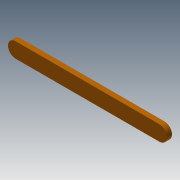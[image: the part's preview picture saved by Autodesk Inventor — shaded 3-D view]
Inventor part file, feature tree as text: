
AUTODESK INVENTOR PART (.ipt)
format: ipt  version: 2013 (Build 170138000, 138)  size: 194,560 bytes
history: native  units: mm
features: sketch x13, extrude x12
ambient origin geometry x8: Origin, YZ Plane, XZ Plane, XY Plane, X Axis, Y Axis, Z Axis, Center Point
bodies: Solid1 (feature_tree)
feature tree (25):
  sketch  "Sketch1"  dims[d6=57.0mm d7=6.0mm]
  extrude  "Extrusion1"  Depth=6.0mm
  extrude  "Extrusion2"  Depth=10.0mm
  extrude  "Extrusion3"  Depth=8.0mm
  extrude  "Extrusion4"  Depth=1.0mm TaperAngle=0.0deg
  extrude  "Extrusion5"  Depth=3.0mm
  sketch  "Sketch7"  dims[d24=2.0mm d25=0.0mm d26=7.0mm d27=0.0mm]
  extrude  "Extrusion6"  Depth=2.0mm TaperAngle=0.0deg
  extrude  "Extrusion7"  Depth=7.0mm TaperAngle=0.0deg
  extrude  "Extrusion8"  Depth=8.0mm
  extrude  "Extrusion9"  Depth=7.0mm
  extrude  "Extrusion10"  Depth=0.01mm
  sketch  "Sketch12"  dims[d39=6.0mm d40=0.01mm]
  extrude  "Extrusion11"  Depth=0.01mm
  extrude  "Extrusion12"  Depth=0.01mm
  sketch  "Sketch2"  dims[d8=2.0mm d9=0.0mm d10=10.0mm]
  sketch  "Sketch3"  dims[d11=7.0mm d12=0.0mm d13=8.0mm]
  sketch  "Sketch4"  dims[d14=7.0mm d15=0.0mm d16=1.0mm d17=0.0mm]
  sketch  "Sketch5"  dims[d18=1.0mm d19=0.0mm d20=3.0mm]
  sketch  "Sketch6"  dims[d21=3.0mm d22=2.0mm d23=0.0mm]
  sketch  "Sketch8"  dims[d28=8.0mm d29=0.0mm d32=8.0mm]
  sketch  "Sketch9"  dims[d33=7.0mm d34=7.0mm]
  sketch  "Sketch10"  dims[d35=17.5mm d36=0.01mm]
  sketch  "Sketch11"  dims[d37=6.0mm d38=0.01mm]
  sketch  "Sketch13"  dims[d41=6.0mm d42=0.01mm d43=6.0mm d44=2.0mm d45=0.0mm d46=0.01mm d47=0.01mm d48=2.0mm d49=0.0mm d50=2.0mm d51=0.0mm]
